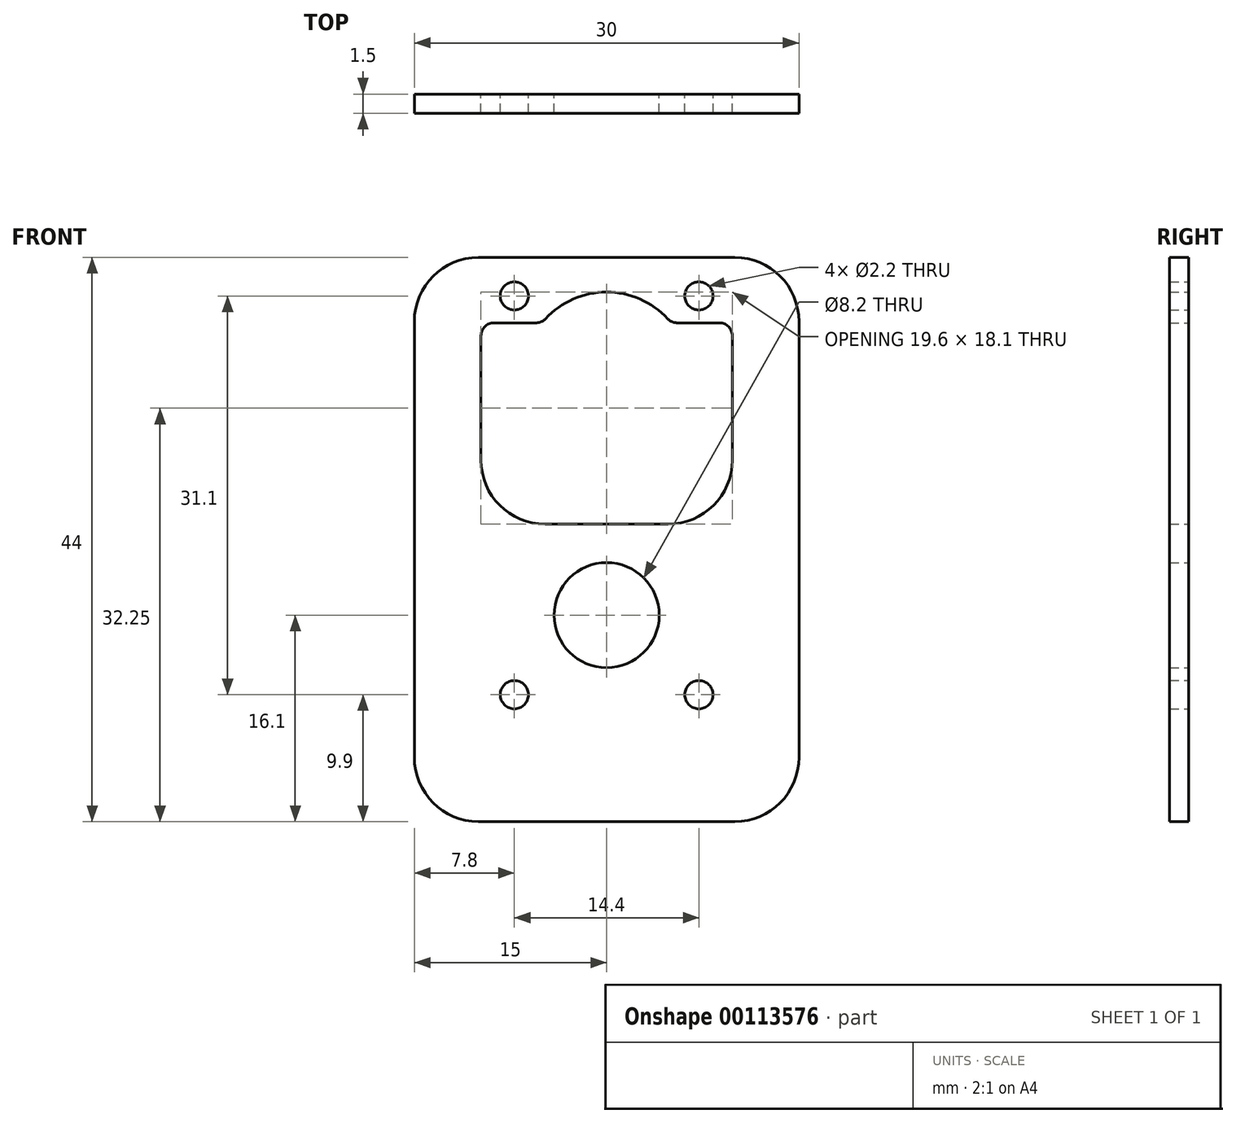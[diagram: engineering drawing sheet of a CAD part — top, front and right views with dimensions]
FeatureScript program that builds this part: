
annotation { "Feature Type Name" : "Feature", "Feature Type Description" : "" }
export const myFeature = defineFeature(function(context is Context, id is Id, definition is map)
    precondition{}
    {
        {
            var Q0;
            Q0=qCreatedBy(makeId("Top.planeOp"),FACE);
            var sketch = newSketch(context, id + "F0", { "sketchPlane" : qUnion([Q0])});
            skLineSegment(sketch, "E0.bottom", {"start": v(37.2, -19.8) * mm, "end": v(-37.2, -19.8) * mm});
            skLineSegment(sketch, "E0.top", {"start": v(37.2, 19.8) * mm, "end": v(-37.2, 19.8) * mm});
            skLineSegment(sketch, "E0.left", {"start": v(37.2, -19.8) * mm, "end": v(37.2, 19.8) * mm});
            skLineSegment(sketch, "E0.right", {"start": v(-37.2, -19.8) * mm, "end": v(-37.2, 19.8) * mm});
            skPoint(sketch, "E0.middle", {"position": v(0, 0) * mm});
            skCircle(sketch, "E1", {"center": v(25, 8.6) * mm, "radius": 4.1 * mm, "construction": true});
            skCircle(sketch, "E2", {"center": v(32.2, 14.8) * mm, "radius": 1 * mm});
            skLineSegment(sketch, "E3.bottom", {"start": v(33.8, -14.6) * mm, "end": v(30.12, -14.6) * mm, "construction": true});
            skLineSegment(sketch, "E3.top", {"start": v(29.8, 1.1) * mm, "end": v(20.2, 1.1) * mm, "construction": true});
            skLineSegment(sketch, "E3.left", {"start": v(34.8, -13.6) * mm, "end": v(34.8, -3.9) * mm, "construction": true});
            skLineSegment(sketch, "E3.right", {"start": v(15.2, -13.6) * mm, "end": v(15.2, -3.9) * mm, "construction": true});
            skPoint(sketch, "E3.middle", {"position": v(25, -6.75) * mm});
            skCircle(sketch, "E4", {"center": v(32.2, -16.8) * mm, "radius": 1 * mm});
            skPoint(sketch, "E5.visualSharp", {"position": v(15.2, 1.1) * mm});
            skArc(sketch, "E5.filletArc", {"start": v(20.2, 1.1) * mm, "mid": v(16.66, -0.36) * mm, "end": v(15.2, -3.9) * mm, "construction": true});
            skPoint(sketch, "E6.visualSharp", {"position": v(34.8, 1.1) * mm});
            skArc(sketch, "E6.filletArc", {"start": v(34.8, -3.9) * mm, "mid": v(33.34, -0.36) * mm, "end": v(29.8, 1.1) * mm, "construction": true});
            skPoint(sketch, "E7.visualSharp", {"position": v(15.2, -14.6) * mm});
            skArc(sketch, "E7.filletArc", {"start": v(15.2, -13.6) * mm, "mid": v(15.5, -14.3) * mm, "end": v(16.2, -14.6) * mm, "construction": true});
            skPoint(sketch, "E8.visualSharp", {"position": v(34.8, -14.6) * mm});
            skArc(sketch, "E8.filletArc", {"start": v(33.8, -14.6) * mm, "mid": v(34.5, -14.3) * mm, "end": v(34.8, -13.6) * mm, "construction": true});
            skArc(sketch, "E9", {"start": v(19.88, -14.6) * mm, "mid": v(25, -17.1) * mm, "end": v(30.12, -14.6) * mm, "construction": true});
            skLineSegment(sketch, "E10.trimOffspring", {"start": v(19.88, -14.6) * mm, "end": v(16.2, -14.6) * mm, "construction": true});
            skLineSegment(sketch, "E11", {"start": v(25, 19.8) * mm, "end": v(25, -19.8) * mm, "construction": true});
            skCircle(sketch, "E12.MirrorC", {"center": v(17.8, 14.8) * mm, "radius": 1 * mm});
            skCircle(sketch, "E13.MirrorC", {"center": v(17.8, -16.8) * mm, "radius": 1 * mm});
            skLineSegment(sketch, "E14", {"start": v(32.2, 14.8) * mm, "end": v(32.2, -16.8) * mm, "construction": true});
            skLineSegment(sketch, "E15", {"start": v(32.2, -1) * mm, "end": v(0, -1) * mm, "construction": true});
            skArc(sketch, "E16.MirrorCS", {"start": v(15.2, 11.6) * mm, "mid": v(15.5, 12.3) * mm, "end": v(16.2, 12.6) * mm});
            skArc(sketch, "E17.MirrorCS", {"start": v(33.8, 12.6) * mm, "mid": v(34.5, 12.3) * mm, "end": v(34.8, 11.6) * mm});
            skLineSegment(sketch, "E18.MirrorCS", {"start": v(15.2, 11.6) * mm, "end": v(15.2, 1.9) * mm});
            skLineSegment(sketch, "E19.MirrorCS", {"start": v(34.8, 11.6) * mm, "end": v(34.8, 1.9) * mm});
            skPoint(sketch, "E20.MirrorP", {"position": v(34.8, -3.1) * mm});
            skArc(sketch, "E21.MirrorCS", {"start": v(19.88, 12.6) * mm, "mid": v(25, 15.1) * mm, "end": v(30.12, 12.6) * mm});
            skPoint(sketch, "E22.MirrorP", {"position": v(15.2, -3.1) * mm});
            skPoint(sketch, "E23.MirrorP", {"position": v(25, 4.75) * mm});
            skCircle(sketch, "E24.MirrorC", {"center": v(25, -10.6) * mm, "radius": 4.1 * mm});
            skArc(sketch, "E25.MirrorCS", {"start": v(20.2, -3.1) * mm, "mid": v(16.66, -1.64) * mm, "end": v(15.2, 1.9) * mm});
            skLineSegment(sketch, "E26.MirrorCS", {"start": v(19.88, 12.6) * mm, "end": v(16.2, 12.6) * mm});
            skArc(sketch, "E27.MirrorCS", {"start": v(34.8, 1.9) * mm, "mid": v(33.34, -1.64) * mm, "end": v(29.8, -3.1) * mm});
            skPoint(sketch, "E28.MirrorP", {"position": v(34.8, 12.6) * mm});
            skLineSegment(sketch, "E29.MirrorCS", {"start": v(29.8, -3.1) * mm, "end": v(20.2, -3.1) * mm});
            skLineSegment(sketch, "E30.MirrorCS", {"start": v(33.8, 12.6) * mm, "end": v(30.12, 12.6) * mm});
            skPoint(sketch, "E31.MirrorP", {"position": v(15.2, 12.6) * mm});
            skArc(sketch, "E32.MirrorCS", {"start": v(-15.2, -13.6) * mm, "mid": v(-15.5, -14.3) * mm, "end": v(-16.2, -14.6) * mm, "construction": true});
            skArc(sketch, "E33.MirrorCS", {"start": v(-33.8, -14.6) * mm, "mid": v(-34.5, -14.3) * mm, "end": v(-34.8, -13.6) * mm, "construction": true});
            skArc(sketch, "E34.MirrorCS", {"start": v(-33.8, 12.6) * mm, "mid": v(-34.5, 12.3) * mm, "end": v(-34.8, 11.6) * mm});
            skArc(sketch, "E35.MirrorCS", {"start": v(-15.2, 11.6) * mm, "mid": v(-15.5, 12.3) * mm, "end": v(-16.2, 12.6) * mm});
            skPoint(sketch, "E36.MirrorP", {"position": v(-34.8, -14.6) * mm});
            skCircle(sketch, "E37.MirrorC", {"center": v(-25, 8.6) * mm, "radius": 4.1 * mm, "construction": true});
            skLineSegment(sketch, "E38.MirrorCS", {"start": v(-15.2, 11.6) * mm, "end": v(-15.2, 1.9) * mm});
            skArc(sketch, "E39.MirrorCS", {"start": v(-19.88, -14.6) * mm, "mid": v(-25, -17.1) * mm, "end": v(-30.12, -14.6) * mm, "construction": true});
            skCircle(sketch, "E40.MirrorC", {"center": v(-32.2, -16.8) * mm, "radius": 1 * mm});
            skLineSegment(sketch, "E41.MirrorCS", {"start": v(-33.8, -14.6) * mm, "end": v(-30.12, -14.6) * mm, "construction": true});
            skLineSegment(sketch, "E42.MirrorCS", {"start": v(-34.8, -13.6) * mm, "end": v(-34.8, -3.9) * mm, "construction": true});
            skCircle(sketch, "E43.MirrorC", {"center": v(-17.8, -16.8) * mm, "radius": 1 * mm});
            skPoint(sketch, "E44.MirrorP", {"position": v(-25, -6.75) * mm});
            skLineSegment(sketch, "E45.MirrorCS", {"start": v(-15.2, -13.6) * mm, "end": v(-15.2, -3.9) * mm, "construction": true});
            skPoint(sketch, "E46.MirrorP", {"position": v(-34.8, 12.6) * mm});
            skLineSegment(sketch, "E47.MirrorCS", {"start": v(-32.2, 14.8) * mm, "end": v(-32.2, -16.8) * mm, "construction": true});
            skLineSegment(sketch, "E48.MirrorCS", {"start": v(-34.8, 11.6) * mm, "end": v(-34.8, 1.9) * mm});
            skLineSegment(sketch, "E49.MirrorCS", {"start": v(-33.8, 12.6) * mm, "end": v(-30.12, 12.6) * mm});
            skArc(sketch, "E50.MirrorCS", {"start": v(-20.2, -3.1) * mm, "mid": v(-16.66, -1.64) * mm, "end": v(-15.2, 1.9) * mm});
            skArc(sketch, "E51.MirrorCS", {"start": v(-19.88, 12.6) * mm, "mid": v(-25, 15.1) * mm, "end": v(-30.12, 12.6) * mm});
            skLineSegment(sketch, "E52.MirrorCS", {"start": v(-19.88, 12.6) * mm, "end": v(-16.2, 12.6) * mm});
            skArc(sketch, "E53.MirrorCS", {"start": v(-34.8, -3.9) * mm, "mid": v(-33.34, -0.36) * mm, "end": v(-29.8, 1.1) * mm, "construction": true});
            skPoint(sketch, "E54.MirrorP", {"position": v(-15.2, 1.1) * mm});
            skCircle(sketch, "E55.MirrorC", {"center": v(-32.2, 14.8) * mm, "radius": 1 * mm});
            skPoint(sketch, "E56.MirrorP", {"position": v(-34.8, 1.1) * mm});
            skPoint(sketch, "E57.MirrorP", {"position": v(-15.2, -3.1) * mm});
            skLineSegment(sketch, "E58.MirrorCS", {"start": v(-29.8, 1.1) * mm, "end": v(-20.2, 1.1) * mm, "construction": true});
            skLineSegment(sketch, "E59.MirrorCS", {"start": v(-29.8, -3.1) * mm, "end": v(-20.2, -3.1) * mm});
            skPoint(sketch, "E60.MirrorP", {"position": v(-34.8, -3.1) * mm});
            skArc(sketch, "E61.MirrorCS", {"start": v(-20.2, 1.1) * mm, "mid": v(-16.66, -0.36) * mm, "end": v(-15.2, -3.9) * mm, "construction": true});
            skCircle(sketch, "E62.MirrorC", {"center": v(-25, -10.6) * mm, "radius": 4.1 * mm});
            skPoint(sketch, "E63.MirrorP", {"position": v(-15.2, -14.6) * mm});
            skPoint(sketch, "E64.MirrorP", {"position": v(-15.2, 12.6) * mm});
            skPoint(sketch, "E65.MirrorP", {"position": v(-25, 4.75) * mm});
            skArc(sketch, "E66.MirrorCS", {"start": v(-34.8, 1.9) * mm, "mid": v(-33.34, -1.64) * mm, "end": v(-29.8, -3.1) * mm});
            skCircle(sketch, "E67.MirrorC", {"center": v(-17.8, 14.8) * mm, "radius": 1 * mm});
            skLineSegment(sketch, "E68.MirrorCS", {"start": v(-19.88, -14.6) * mm, "end": v(-16.2, -14.6) * mm, "construction": true});
            skSolve(sketch);
        }
        {
            var Q0;
            Q0=qSketchRegion(id+"F0",true);
            extrude(context, id + "F1", {"entities" : qUnion([Q0]), "depth" : 1.5 * mm});
        }
        {
            var Q0;
            Q0=qCreatedBy(makeId("Top.planeOp"),FACE);
            var sketch = newSketch(context, id + "F2", { "sketchPlane" : qUnion([Q0])});
            skLineSegment(sketch, "E69.bottom", {"start": v(15, 19.8) * mm, "end": v(-15, 19.8) * mm});
            skLineSegment(sketch, "E69.top", {"start": v(15, 21.3) * mm, "end": v(-15, 21.3) * mm});
            skLineSegment(sketch, "E69.left", {"start": v(15, 19.8) * mm, "end": v(15, 21.3) * mm});
            skLineSegment(sketch, "E69.right", {"start": v(-15, 19.8) * mm, "end": v(-15, 21.3) * mm});
            skPoint(sketch, "E69.middle", {"position": v(0, 20.55) * mm});
            skLineSegment(sketch, "E70.0", {"start": v(37.2, 19.8) * mm, "end": v(-37.2, 19.8) * mm, "construction": true});
            skSolve(sketch);
        }
        {
            var Q0;
            Q0=qSketchRegion(id+"F2",true);
            extrude(context, id + "F3", {"entities" : qUnion([Q0]), "operationType" : NewBodyOperationType.ADD, "depth" : (38 + 6) * mm});
        }
        {
            var Q0;
            Q0=makeQuery(id+"F3.opExtrude","SWEPT_FACE",FACE,{"disambiguationData":[OSD([sQuery(id+"F2.wireOp",EDGE,"E69.top")])]});
            var sketch = newSketch(context, id + "F4", { "sketchPlane" : qUnion([Q0])});
            skLineSegment(sketch, "E71", {"start": v(-15, 22) * mm, "end": v(15, 22) * mm, "construction": true});
            skCircle(sketch, "E72", {"center": v(7.2, 41) * mm, "radius": 1.1 * mm});
            skCircle(sketch, "E73", {"center": v(7.2, 9.9) * mm, "radius": 1.1 * mm});
            skCircle(sketch, "E74", {"center": v(0, 16.1) * mm, "radius": 4.1 * mm});
            skLineSegment(sketch, "E75.bottom", {"start": v(8.8, 38.9) * mm, "end": v(5.5, 38.9) * mm});
            skLineSegment(sketch, "E75.top", {"start": v(4.8, 23.2) * mm, "end": v(-4.8, 23.2) * mm});
            skLineSegment(sketch, "E75.left", {"start": v(9.8, 37.9) * mm, "end": v(9.8, 28.2) * mm});
            skLineSegment(sketch, "E75.right", {"start": v(-9.8, 37.9) * mm, "end": v(-9.8, 28.2) * mm});
            skPoint(sketch, "E75.middle", {"position": v(0, 31.05) * mm});
            skPoint(sketch, "E76.visualSharp", {"position": v(-9.8, 23.2) * mm});
            skArc(sketch, "E76.filletArc", {"start": v(-9.8, 28.2) * mm, "mid": v(-8.34, 24.66) * mm, "end": v(-4.8, 23.2) * mm});
            skPoint(sketch, "E77.visualSharp", {"position": v(9.8, 23.2) * mm});
            skArc(sketch, "E77.filletArc", {"start": v(4.8, 23.2) * mm, "mid": v(8.34, 24.66) * mm, "end": v(9.8, 28.2) * mm});
            skPoint(sketch, "E78.visualSharp", {"position": v(9.8, 38.9) * mm});
            skArc(sketch, "E78.filletArc", {"start": v(9.8, 37.9) * mm, "mid": v(9.5, 38.6) * mm, "end": v(8.8, 38.9) * mm});
            skPoint(sketch, "E79.visualSharp", {"position": v(-9.8, 38.9) * mm});
            skArc(sketch, "E79.filletArc", {"start": v(-8.8, 38.9) * mm, "mid": v(-9.5, 38.6) * mm, "end": v(-9.8, 37.9) * mm});
            skCircle(sketch, "E80.MirrorC", {"center": v(-7.2, 41) * mm, "radius": 1.1 * mm});
            skCircle(sketch, "E81.MirrorC", {"center": v(-7.2, 9.9) * mm, "radius": 1.1 * mm});
            skArc(sketch, "E82", {"start": v(4.77, 39.22) * mm, "mid": v(0, 41.3) * mm, "end": v(-4.77, 39.22) * mm});
            skLineSegment(sketch, "E83.trimOffspring", {"start": v(-5.5, 38.9) * mm, "end": v(-8.8, 38.9) * mm});
            skPoint(sketch, "E84.visualSharp", {"position": v(-5.04, 38.9) * mm});
            skArc(sketch, "E84.filletArc", {"start": v(-5.5, 38.9) * mm, "mid": v(-5.1, 38.98) * mm, "end": v(-4.77, 39.22) * mm});
            skPoint(sketch, "E85.visualSharp", {"position": v(5.04, 38.9) * mm});
            skArc(sketch, "E85.filletArc", {"start": v(4.77, 39.22) * mm, "mid": v(5.1, 38.98) * mm, "end": v(5.5, 38.9) * mm});
            skSolve(sketch);
        }
        {
            var Q0;
            Q0=qSketchRegion(id+"F4",true);
            extrude(context, id + "F5", {"entities" : qUnion([Q0]), "operationType" : NewBodyOperationType.REMOVE, "endBound" : BoundingType.UP_TO_NEXT, "oppositeDirection" : true, "depth" : 25 * mm});
        }
        {
            var Q0;
            Q0=makeQuery(id+"F1.opExtrude","SWEPT_EDGE",EDGE,{"disambiguationData":[OSD([sQuery(id+"F0.wireOp",EDGE,"E0.top"),sQuery(id+"F0.wireOp",EDGE,"E0.right")])]});
            var Q1;
            Q1=makeQuery(id+"F1.opExtrude","SWEPT_EDGE",EDGE,{"disambiguationData":[OSD([sQuery(id+"F0.wireOp",EDGE,"E0.bottom"),sQuery(id+"F0.wireOp",EDGE,"E0.right")])]});
            var Q2;
            Q2=makeQuery(id+"F1.opExtrude","SWEPT_EDGE",EDGE,{"disambiguationData":[OSD([sQuery(id+"F0.wireOp",EDGE,"E0.top"),sQuery(id+"F0.wireOp",EDGE,"E0.left")])]});
            var Q3;
            Q3=makeQuery(id+"F1.opExtrude","SWEPT_EDGE",EDGE,{"disambiguationData":[OSD([sQuery(id+"F0.wireOp",EDGE,"E0.bottom"),sQuery(id+"F0.wireOp",EDGE,"E0.left")])]});
            var Q4;
            Q4=makeQuery(id+"F3.opExtrude","CAP_EDGE",EDGE,{"disambiguationData":[OSD([sQuery(id+"F2.wireOp",EDGE,"E69.right")])],"isStart":false});
            var Q5;
            Q5=makeQuery(id+"F3.opExtrude","CAP_EDGE",EDGE,{"disambiguationData":[OSD([sQuery(id+"F2.wireOp",EDGE,"E69.left")])],"isStart":false});
            fillet(context, id + "F6", {"entities" : qUnion([Q0, Q1, Q2, Q3, Q4, Q5]), "radius" : 5 * mm, "tangentPropagation" : true, "allowEdgeOverflow" : false});
        }
        {
            var Q0;
            Q0=makeQuery(id+"F1.opExtrude","CAP_FACE",FACE,{"disambiguationData":[OSD([sQuery(id+"F0.wireOp",EDGE,"E0.bottom"),sQuery(id+"F0.wireOp",EDGE,"E0.top"),sQuery(id+"F0.wireOp",EDGE,"E0.left"),sQuery(id+"F0.wireOp",EDGE,"E0.right"),sQuery(id+"F0.wireOp",EDGE,"E2"),sQuery(id+"F0.wireOp",EDGE,"E4"),sQuery(id+"F0.wireOp",EDGE,"E12.MirrorC"),sQuery(id+"F0.wireOp",EDGE,"E13.MirrorC"),sQuery(id+"F0.wireOp",EDGE,"E16.MirrorCS"),sQuery(id+"F0.wireOp",EDGE,"E17.MirrorCS"),sQuery(id+"F0.wireOp",EDGE,"E18.MirrorCS"),sQuery(id+"F0.wireOp",EDGE,"E19.MirrorCS"),sQuery(id+"F0.wireOp",EDGE,"E21.MirrorCS"),sQuery(id+"F0.wireOp",EDGE,"E24.MirrorC"),sQuery(id+"F0.wireOp",EDGE,"E25.MirrorCS"),sQuery(id+"F0.wireOp",EDGE,"E26.MirrorCS"),sQuery(id+"F0.wireOp",EDGE,"E27.MirrorCS"),sQuery(id+"F0.wireOp",EDGE,"E29.MirrorCS"),sQuery(id+"F0.wireOp",EDGE,"E30.MirrorCS"),sQuery(id+"F0.wireOp",EDGE,"E34.MirrorCS"),sQuery(id+"F0.wireOp",EDGE,"E35.MirrorCS"),sQuery(id+"F0.wireOp",EDGE,"E38.MirrorCS"),sQuery(id+"F0.wireOp",EDGE,"E40.MirrorC"),sQuery(id+"F0.wireOp",EDGE,"E43.MirrorC"),sQuery(id+"F0.wireOp",EDGE,"E48.MirrorCS"),sQuery(id+"F0.wireOp",EDGE,"E49.MirrorCS"),sQuery(id+"F0.wireOp",EDGE,"E50.MirrorCS"),sQuery(id+"F0.wireOp",EDGE,"E51.MirrorCS"),sQuery(id+"F0.wireOp",EDGE,"E52.MirrorCS"),sQuery(id+"F0.wireOp",EDGE,"E55.MirrorC"),sQuery(id+"F0.wireOp",EDGE,"E59.MirrorCS"),sQuery(id+"F0.wireOp",EDGE,"E62.MirrorC"),sQuery(id+"F0.wireOp",EDGE,"E66.MirrorCS"),sQuery(id+"F0.wireOp",EDGE,"E67.MirrorC")])],"isStart":false});
            var sketch = newSketch(context, id + "F7", { "sketchPlane" : qUnion([Q0])});
            skLineSegment(sketch, "E86.bottom", {"start": v(-37.2, 19.8) * mm, "end": v(37.2, 19.8) * mm});
            skLineSegment(sketch, "E86.top", {"start": v(-37.2, -19.8) * mm, "end": v(37.2, -19.8) * mm});
            skLineSegment(sketch, "E86.left", {"start": v(-37.2, 19.8) * mm, "end": v(-37.2, -19.8) * mm});
            skLineSegment(sketch, "E86.right", {"start": v(37.2, 19.8) * mm, "end": v(37.2, -19.8) * mm});
            skPoint(sketch, "E86.middle", {"position": v(0, 0) * mm});
            skSolve(sketch);
        }
        {
            var Q0;
            Q0 = qSketchRegion(id + "F7", true);
            extrude(context, id + "F8", {"entities" : qUnion([Q0]), "operationType" : NewBodyOperationType.REMOVE, "endBound" : BoundingType.UP_TO_NEXT, "oppositeDirection" : true, "depth" : 25 * mm});
        }
        {
            var Q0;
            Q0=makeQuery(id+"F3.opExtrude","CAP_EDGE",EDGE,{"disambiguationData":[OSD([sQuery(id+"F2.wireOp",EDGE,"E69.right")])],"isStart":true});
            var Q1;
            Q1=makeQuery(id+"F3.opExtrude","CAP_EDGE",EDGE,{"disambiguationData":[OSD([sQuery(id+"F2.wireOp",EDGE,"E69.left")])],"isStart":true});
            fillet(context, id + "F9", {"entities" : qUnion([Q0, Q1]), "radius" : 5 * mm, "tangentPropagation" : true, "allowEdgeOverflow" : false});
        }
    });
